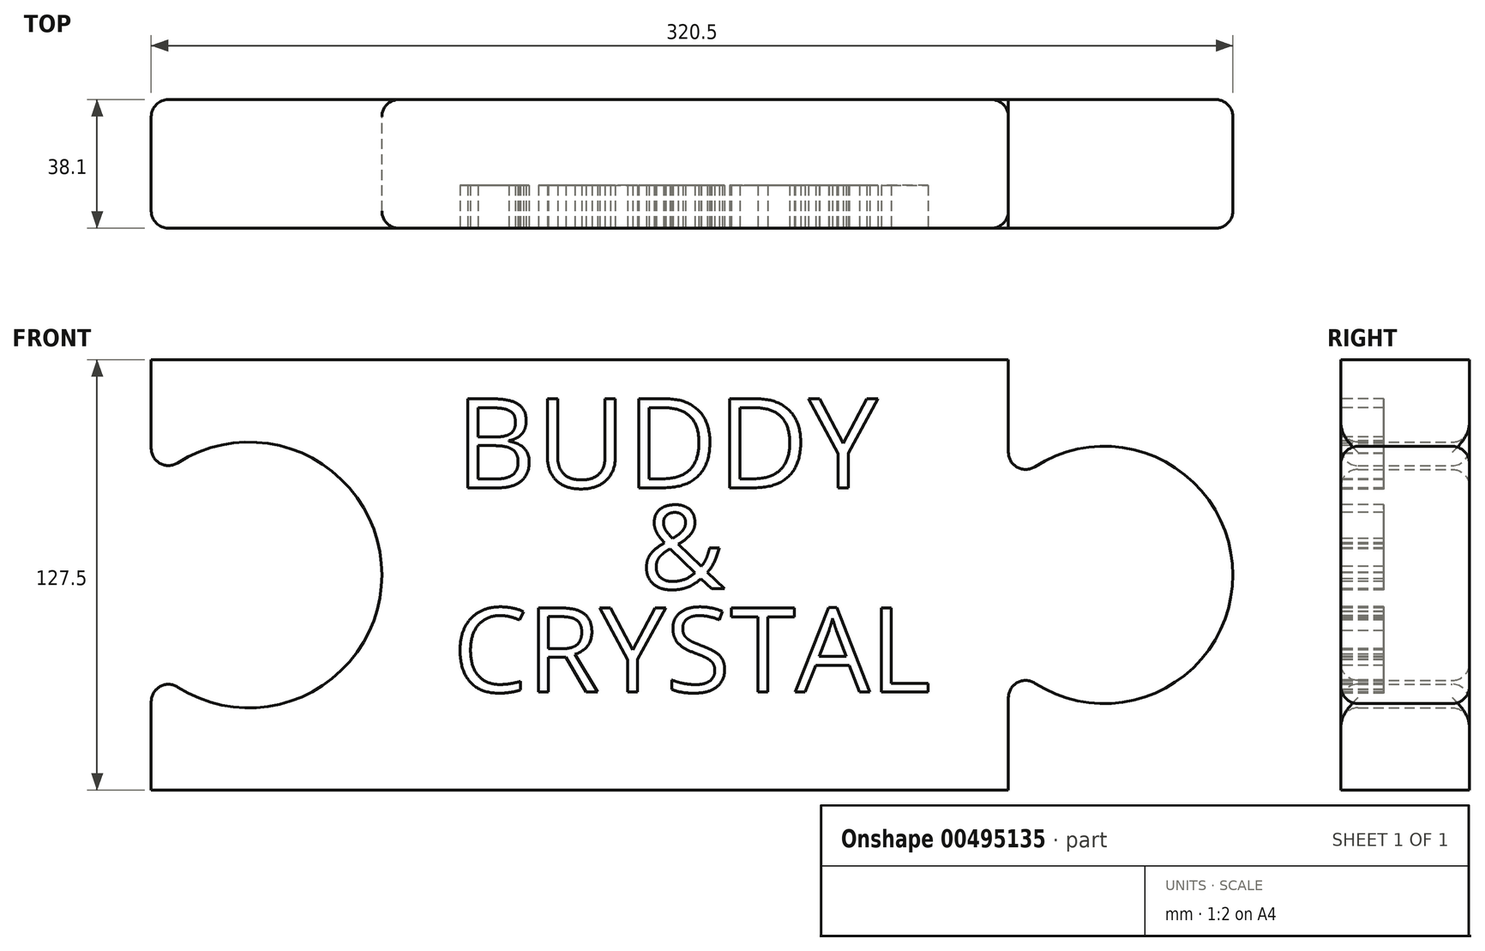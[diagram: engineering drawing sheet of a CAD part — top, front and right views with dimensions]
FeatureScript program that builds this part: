
annotation { "Feature Type Name" : "Feature", "Feature Type Description" : "" }
export const myFeature = defineFeature(function(context is Context, id is Id, definition is map)
    precondition{}
    {
        {
            var Q0;
            Q0=qCreatedBy(makeId("Front.planeOp"),FACE);
            var sketch = newSketch(context, id + "F0", { "sketchPlane" : qUnion([Q0])});
            skLineSegment(sketch, "E0", {"start": v(-190.12, 83) * mm, "end": v(63.88, 83) * mm});
            skLineSegment(sketch, "E1", {"start": v(-190.12, -44.5) * mm, "end": v(63.88, -44.5) * mm});
            skArc(sketch, "E2", {"start": v(63.88, -6.15) * mm, "mid": v(130.38, 19.25) * mm, "end": v(63.88, 44.65) * mm});
            skLineSegment(sketch, "E3", {"start": v(63.88, 44.65) * mm, "end": v(63.88, 83) * mm});
            skLineSegment(sketch, "E4", {"start": v(63.88, -6.15) * mm, "end": v(63.88, -44.5) * mm});
            skArc(sketch, "E5", {"start": v(-190.12, -7.42) * mm, "mid": v(-121.79, 19.25) * mm, "end": v(-190.12, 45.92) * mm});
            skLineSegment(sketch, "E6", {"start": v(-190.12, -7.42) * mm, "end": v(-190.12, -44.5) * mm});
            skLineSegment(sketch, "E7", {"start": v(-190.12, 45.92) * mm, "end": v(-190.12, 83) * mm});
            skSolve(sketch);
        }
        {
            var Q0;
            Q0 = qSketchRegion(id + "F0", true);
            extrude(context, id + "F1", {"entities" : qUnion([Q0]), "depth" : 38.1 * mm});
        }
        {
            var Q0;
            Q0=makeQuery(id+"F1.opExtrude","CAP_EDGE",EDGE,{"disambiguationData":[OSD([sQuery(id+"F0.wireOp",EDGE,"E5")])],"isStart":true});
            var Q1;
            Q1=makeQuery(id+"F1.opExtrude","SWEPT_EDGE",EDGE,{"disambiguationData":[OSD([sQuery(id+"F0.wireOp",EDGE,"E5"),sQuery(id+"F0.wireOp",EDGE,"E7")])]});
            var Q2;
            Q2=makeQuery(id+"F1.opExtrude","CAP_EDGE",EDGE,{"disambiguationData":[OSD([sQuery(id+"F0.wireOp",EDGE,"E7")])],"isStart":true});
            var Q3;
            Q3=makeQuery(id+"F1.opExtrude","CAP_EDGE",EDGE,{"disambiguationData":[OSD([sQuery(id+"F0.wireOp",EDGE,"E7")])],"isStart":false});
            var Q4;
            Q4=makeQuery(id+"F1.opExtrude","SWEPT_EDGE",EDGE,{"disambiguationData":[OSD([sQuery(id+"F0.wireOp",EDGE,"E5"),sQuery(id+"F0.wireOp",EDGE,"E6")])]});
            var Q5;
            Q5=makeQuery(id+"F1.opExtrude","CAP_EDGE",EDGE,{"disambiguationData":[OSD([sQuery(id+"F0.wireOp",EDGE,"E6")])],"isStart":true});
            var Q6;
            Q6=makeQuery(id+"F1.opExtrude","CAP_EDGE",EDGE,{"disambiguationData":[OSD([sQuery(id+"F0.wireOp",EDGE,"E6")])],"isStart":false});
            var Q7;
            Q7=makeQuery(id+"F1.opExtrude","SWEPT_FACE",FACE,{"disambiguationData":[OSD([sQuery(id+"F0.wireOp",EDGE,"E5")])]});
            var Q8;
            Q8=makeQuery(id+"F1.opExtrude","SWEPT_FACE",FACE,{"disambiguationData":[OSD([sQuery(id+"F0.wireOp",EDGE,"E2")])]});
            fillet(context, id + "F2", {"entities" : qUnion([Q0, Q1, Q2, Q3, Q4, Q5, Q6, Q7, Q8]), "radius" : 5.08 * mm, "tangentPropagation" : true, "allowEdgeOverflow" : false});
        }
        {
            var Q0;
            Q0=makeQuery(id+"F1.opExtrude","CAP_FACE",FACE,{"disambiguationData":[OSD([sQuery(id+"F0.wireOp",EDGE,"E0"),sQuery(id+"F0.wireOp",EDGE,"E1"),sQuery(id+"F0.wireOp",EDGE,"E2"),sQuery(id+"F0.wireOp",EDGE,"E3"),sQuery(id+"F0.wireOp",EDGE,"E4"),sQuery(id+"F0.wireOp",EDGE,"E5"),sQuery(id+"F0.wireOp",EDGE,"E6"),sQuery(id+"F0.wireOp",EDGE,"E7")])],"isStart":false});
            var sketch = newSketch(context, id + "F3", { "sketchPlane" : qUnion([Q0])});
            skText(sketch, "E8", { "text": "BUDDY", "fontName": "OpenSans-Regular.ttf"});
            skText(sketch, "E9", { "text": "CRYSTAL", "fontName": "OpenSans-Regular.ttf"});
            skText(sketch, "E10", { "text": "&", "fontName": "OpenSans-Regular.ttf"});
            const initialGuessF3  = {"E8": [-0.1, 0.04508, 1, 0, 0.02657], "E9": [-0.10074, -0.01544, 1, 0, 0.0251], "E10": [-0.04527, 0.01516, 1, 0, 0.02473]};
            skSetInitialGuess(sketch, initialGuessF3);
            skSolve(sketch);
        }
        {
            var Q0;
            Q0 = qSketchRegion(id + "F3", true);
            extrude(context, id + "F4", {"entities" : qUnion([Q0]), "operationType" : NewBodyOperationType.REMOVE, "oppositeDirection" : true, "depth" : 12.7 * mm});
        }
    });
